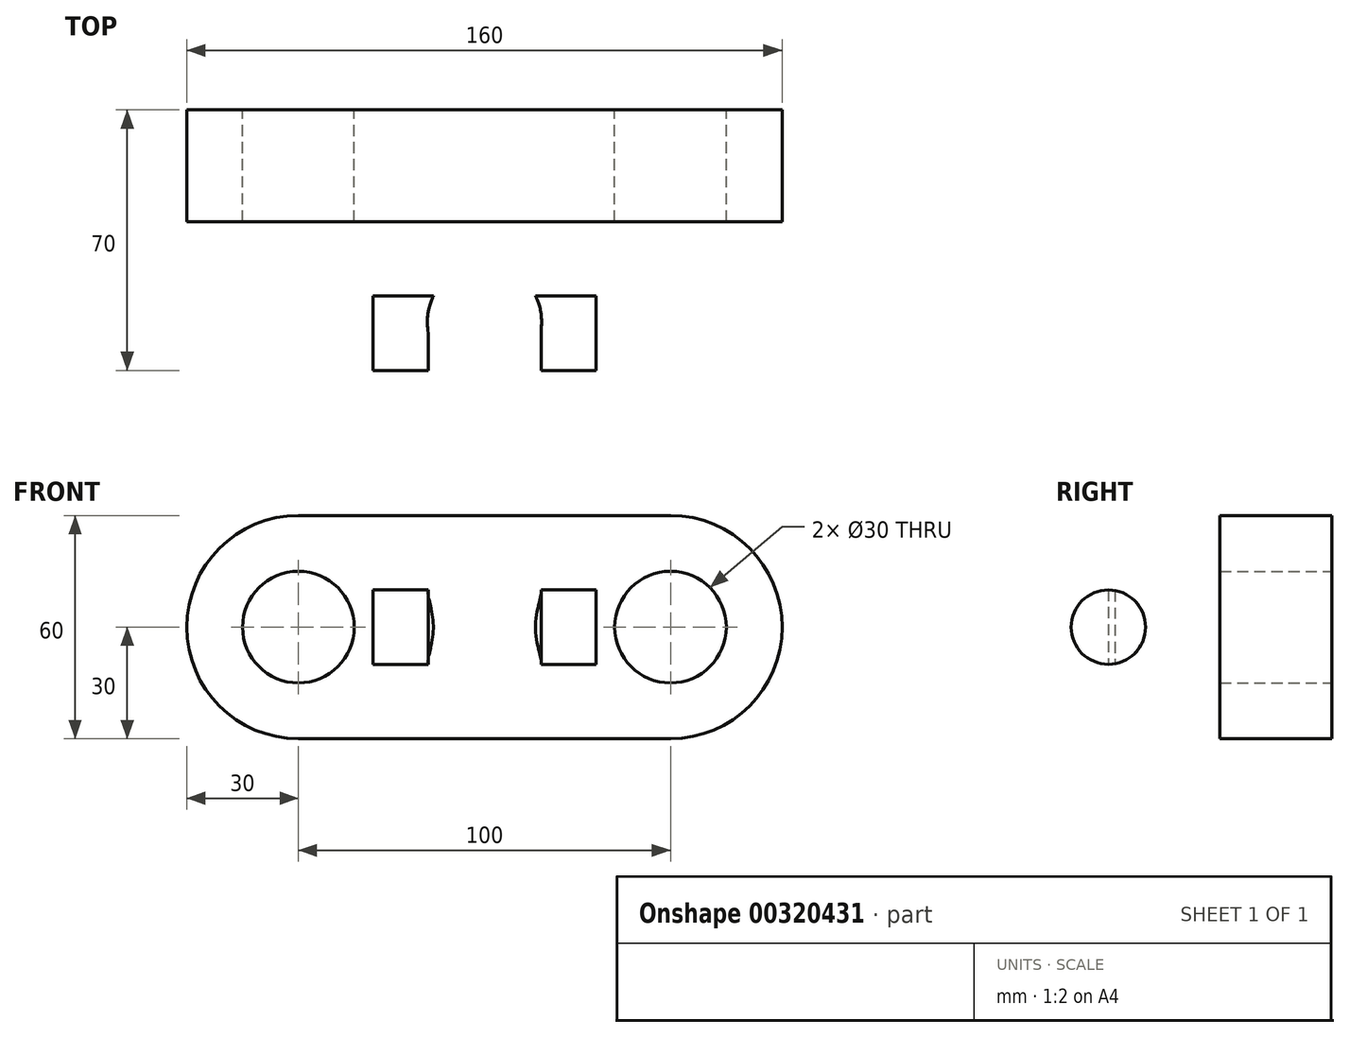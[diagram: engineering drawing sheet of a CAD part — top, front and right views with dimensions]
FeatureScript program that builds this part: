
annotation { "Feature Type Name" : "Feature", "Feature Type Description" : "" }
export const myFeature = defineFeature(function(context is Context, id is Id, definition is map)
    precondition{}
    {
        {
            var Q0;
            Q0=qCreatedBy(makeId("Front.planeOp"),FACE);
            var sketch = newSketch(context, id + "F0", { "sketchPlane" : qUnion([Q0])});
            skCircle(sketch, "E0", {"center": v(-50, 0) * mm, "radius": 15 * mm});
            skCircle(sketch, "E1", {"center": v(50, 0) * mm, "radius": 15 * mm});
            skArc(sketch, "E2", {"start": v(-50, 30) * mm, "mid": v(-80, 0) * mm, "end": v(-50, -30) * mm});
            skArc(sketch, "E3", {"start": v(50, -30) * mm, "mid": v(80, 0) * mm, "end": v(50, 30) * mm});
            skLineSegment(sketch, "E4", {"start": v(-50, 30) * mm, "end": v(50, 30) * mm});
            skLineSegment(sketch, "E5", {"start": v(-50, -30) * mm, "end": v(50, -30) * mm});
            skPoint(sketch, "E6.orphan", {"position": v(-118.51, 0) * mm});
            skLineSegment(sketch, "E7", {"start": v(-93.82, 0) * mm, "end": v(97.69, 0) * mm});
            skSolve(sketch);
        }
        {
            var Q0;
            Q0=makeQuery(id+"F0.imprint","IMPRINT",FACE,{"disambiguationData":[TD([[makeQuery(id+"F0.imprint","IMPRINT",EDGE,{"derivedFrom":sQuery(id+"F0.wireOp",EDGE,"E3")}),1.0]])]});
            extrude(context, id + "F1", {"entities" : qUnion([Q0]), "endBound" : BoundingType.SYMMETRIC, "depth" : 30 * mm});
        }
        {
            var Q0;
            Q0=qCreatedBy(makeId("Top.planeOp"),FACE);
            var sketch = newSketch(context, id + "F2", { "sketchPlane" : qUnion([Q0])});
            skLineSegment(sketch, "E8.bottom", {"start": v(-30, -65) * mm, "end": v(-15.04, -65) * mm});
            skLineSegment(sketch, "E8.top", {"start": v(-30, -15) * mm, "end": v(30, -15) * mm});
            skLineSegment(sketch, "E8.left", {"start": v(-30, -65) * mm, "end": v(-30, -15) * mm});
            skLineSegment(sketch, "E8.right", {"start": v(30, -65) * mm, "end": v(30, -15) * mm});
            skPoint(sketch, "E9.centerSnap0", {"position": v(0, -65) * mm});
            skArc(sketch, "E10", {"start": v(15.29, -43.27) * mm, "mid": v(-0.86, -26.54) * mm, "end": v(-15.04, -44.97) * mm});
            skPoint(sketch, "E10.centerSnap0", {"position": v(0, -15) * mm});
            skLineSegment(sketch, "E11", {"start": v(-15.04, -38.77) * mm, "end": v(-15.04, -65) * mm});
            skLineSegment(sketch, "E12", {"start": v(15.29, -40.47) * mm, "end": v(15.29, -65) * mm});
            skLineSegment(sketch, "E13.trimOffspring", {"start": v(15.29, -65) * mm, "end": v(30, -65) * mm});
            skSolve(sketch);
        }
        {
            var Q0;
            {var subQ0=sQuery(id+"F2.wireOp",EDGE,"E8.bottom");Q0=makeQuery(id+"F2.imprint","IMPRINT",FACE,{"disambiguationData":[TD([[makeQuery(id+"F2.imprint","IMPRINT",EDGE,{"derivedFrom":subQ0}),1.0]])]});}
            extrude(context, id + "F3", {"entities" : qUnion([Q0]), "operationType" : NewBodyOperationType.ADD, "endBound" : BoundingType.SYMMETRIC, "depth" : 40 * mm});
        }
        {
            var Q0;
            Q0=makeQuery(id+"F3.opExtrude","SWEPT_FACE",FACE,{"disambiguationData":[OSD([sQuery(id+"F2.wireOp",EDGE,"E8.left")])]});
            var sketch = newSketch(context, id + "F4", { "sketchPlane" : qUnion([Q0])});
            skLineSegment(sketch, "E14", {"start": v(45, 43.61) * mm, "end": v(45, -50.76) * mm});
            skArc(sketch, "E15", {"start": v(45, -20) * mm, "mid": v(65, 0) * mm, "end": v(45, 20) * mm});
            skSolve(sketch);
        }
        {
            var Q0;
            {var subQ0=sQuery(id+"F4.wireOp",EDGE,"E15");var subQ1=sQuery(id+"F2.wireOp",EDGE,"E8.left");var subQ2=makeQuery(id+"F3.opExtrude","CAP_EDGE",EDGE,{"disambiguationData":[OSD([subQ1])],"isStart":false});var subQ3=makeQuery(id+"F4.imprint","INTERSECT",VERTEX,{"derivedFrom":[subQ2,sQuery(id+"F4.wireOp",EDGE,"E14"),subQ0]});Q0=makeQuery(id+"F4.imprint","IMPRINT",FACE,{"disambiguationData":[TD([[makeQuery(id+"F4.imprint","IMPRINT",EDGE,{"disambiguationData":[TD([[subQ3,1.0]])],"derivedFrom":subQ0}),-1.0]])]});}
            var Q1;
            {var subQ0=sQuery(id+"F4.wireOp",EDGE,"E15");var subQ1=sQuery(id+"F2.wireOp",EDGE,"E8.left");var subQ2=makeQuery(id+"F3.opExtrude","CAP_EDGE",EDGE,{"disambiguationData":[OSD([subQ1])],"isStart":true});var subQ3=makeQuery(id+"F4.imprint","INTERSECT",VERTEX,{"derivedFrom":[subQ2,sQuery(id+"F4.wireOp",EDGE,"E14"),subQ0]});Q1=makeQuery(id+"F4.imprint","IMPRINT",FACE,{"disambiguationData":[TD([[makeQuery(id+"F4.imprint","IMPRINT",EDGE,{"disambiguationData":[TD([[subQ3,-1.0]])],"derivedFrom":subQ0}),-1.0]])]});}
            extrude(context, id + "F5", {"entities" : qUnion([Q0, Q1]), "operationType" : NewBodyOperationType.REMOVE, "endBound" : BoundingType.THROUGH_ALL, "oppositeDirection" : true, "depth" : 25 * mm});
        }
        {
            var Q0;
            Q0=makeQuery(id+"F3.opExtrude","SWEPT_FACE",FACE,{"disambiguationData":[OSD([sQuery(id+"F2.wireOp",EDGE,"E8.left")])]});
            var sketch = newSketch(context, id + "F6", { "sketchPlane" : qUnion([Q0])});
            skLineSegment(sketch, "E16", {"start": v(45, 31.2) * mm, "end": v(45, -24.26) * mm});
            skCircle(sketch, "E17", {"center": v(45, 0) * mm, "radius": 10 * mm});
            skSolve(sketch);
        }
        {
            var Q0;
            {var subQ0=sQuery(id+"F6.wireOp",EDGE,"E17");var subQ1=sQuery(id+"F6.wireOp",EDGE,"E16");var subQ2=makeQuery(id+"F6.imprint","INTERSECT",VERTEX,{"disambiguationData":[OD(0.0)],"derivedFrom":[subQ1,subQ0]});Q0=makeQuery(id+"F6.imprint","IMPRINT",FACE,{"disambiguationData":[TD([[makeQuery(id+"F6.imprint","IMPRINT",EDGE,{"disambiguationData":[TD([[subQ2,-1.0]])],"derivedFrom":subQ1}),1.0]])]});}
            var Q1;
            {var subQ0=sQuery(id+"F6.wireOp",EDGE,"E17");var subQ1=sQuery(id+"F6.wireOp",EDGE,"E16");var subQ2=makeQuery(id+"F6.imprint","INTERSECT",VERTEX,{"disambiguationData":[OD(0.0)],"derivedFrom":[subQ1,subQ0]});Q1=makeQuery(id+"F6.imprint","IMPRINT",FACE,{"disambiguationData":[TD([[makeQuery(id+"F6.imprint","IMPRINT",EDGE,{"disambiguationData":[TD([[subQ2,-1.0]])],"derivedFrom":subQ1}),-1.0]])]});}
            extrude(context, id + "F7", {"entities" : qUnion([Q0, Q1]), "operationType" : NewBodyOperationType.REMOVE, "endBound" : BoundingType.THROUGH_ALL, "oppositeDirection" : true, "depth" : 25 * mm});
        }
    });
